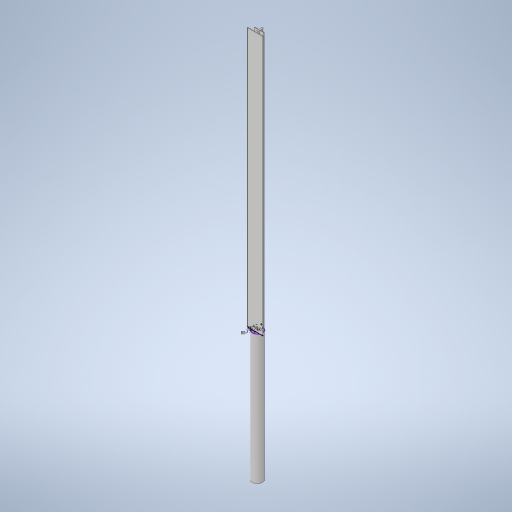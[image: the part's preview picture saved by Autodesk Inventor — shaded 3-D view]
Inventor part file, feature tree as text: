
AUTODESK INVENTOR PART (.ipt)
format: ipt  version: 2024 (Build 280153000, 153)  size: 270,848 bytes
history: native  units: mm
features: extrude x2, sketch x1
ambient origin geometry x8: Origin, YZ Plane, XZ Plane, XY Plane, X Axis, Y Axis, Z Axis, Center Point
bodies: Solid1 (feature_tree)
feature tree (3):
  sketch  "Sketch1"  dims[d0=60.0mm d1=60.0mm d2=5.0mm d3=4.0mm d4=30.0mm d5=4.0mm d6=25.0mm d7=2000.0mm d8=0.0mm d9=80.0mm d10=3.0mm d11=1000.0mm d12=0.0mm]
  extrude  "Extrusion1"  Depth=60.0mm
  extrude  "Extrusion2"  Depth=5.0mm
